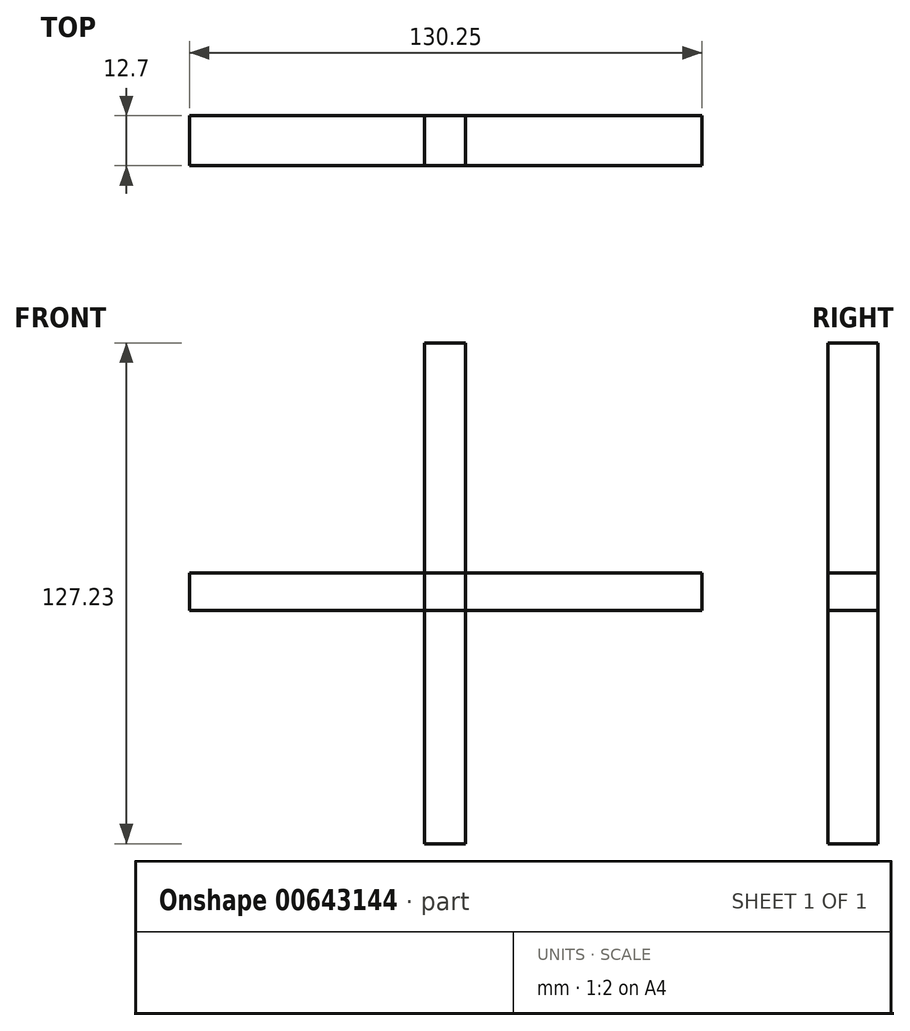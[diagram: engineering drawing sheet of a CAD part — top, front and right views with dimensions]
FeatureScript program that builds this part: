
annotation { "Feature Type Name" : "Feature", "Feature Type Description" : "" }
export const myFeature = defineFeature(function(context is Context, id is Id, definition is map)
    precondition{}
    {
        {
            var Q0;
            Q0=qCreatedBy(makeId("Front.planeOp"),FACE);
            var sketch = newSketch(context, id + "F0", { "sketchPlane" : qUnion([Q0])});
            skLineSegment(sketch, "E0.bottom", {"start": v(10.38, 0) * mm, "end": v(0, 0) * mm});
            skLineSegment(sketch, "E0.top", {"start": v(10.38, 58.5) * mm, "end": v(0, 58.5) * mm});
            skLineSegment(sketch, "E0.left", {"start": v(10.38, 0) * mm, "end": v(10.38, 58.5) * mm});
            skLineSegment(sketch, "E0.right", {"start": v(0, 0) * mm, "end": v(0, 58.5) * mm});
            skLineSegment(sketch, "E1.bottom", {"start": v(10.38, 0) * mm, "end": v(70.54, 0) * mm});
            skLineSegment(sketch, "E1.top", {"start": v(10.38, -9.47) * mm, "end": v(70.54, -9.47) * mm});
            skLineSegment(sketch, "E1.left", {"start": v(10.38, 0) * mm, "end": v(10.38, -9.47) * mm});
            skLineSegment(sketch, "E1.right", {"start": v(70.54, 0) * mm, "end": v(70.54, -9.47) * mm});
            skLineSegment(sketch, "E2.bottom", {"start": v(10.38, -9.47) * mm, "end": v(0, -9.47) * mm});
            skLineSegment(sketch, "E2.top", {"start": v(10.38, -68.73) * mm, "end": v(0, -68.73) * mm});
            skLineSegment(sketch, "E2.left", {"start": v(10.38, -9.47) * mm, "end": v(10.38, -68.73) * mm});
            skLineSegment(sketch, "E2.right", {"start": v(0, -9.47) * mm, "end": v(0, -68.73) * mm});
            skLineSegment(sketch, "E3.bottom", {"start": v(0, -9.47) * mm, "end": v(-59.7, -9.47) * mm});
            skLineSegment(sketch, "E3.top", {"start": v(0, 0) * mm, "end": v(-59.7, 0) * mm});
            skLineSegment(sketch, "E3.left", {"start": v(0, -9.47) * mm, "end": v(0, 0) * mm});
            skLineSegment(sketch, "E3.right", {"start": v(-59.7, -9.47) * mm, "end": v(-59.7, 0) * mm});
            skSolve(sketch);
        }
        {
            var Q0;
            Q0=makeQuery(id+"F0.imprint","IMPRINT",FACE,{"disambiguationData":[TD([[makeQuery(id+"F0.imprint","IMPRINT",EDGE,{"derivedFrom":sQuery(id+"F0.wireOp",EDGE,"E3.bottom")}),-1.0]])]});
            var Q1;
            Q1=makeQuery(id+"F0.imprint","IMPRINT",FACE,{"disambiguationData":[TD([[makeQuery(id+"F0.imprint","IMPRINT",EDGE,{"derivedFrom":sQuery(id+"F0.wireOp",EDGE,"E0.bottom")}),-1.0]])]});
            var Q2;
            Q2=makeQuery(id+"F0.imprint","IMPRINT",FACE,{"disambiguationData":[TD([[makeQuery(id+"F0.imprint","IMPRINT",EDGE,{"derivedFrom":sQuery(id+"F0.wireOp",EDGE,"E1.bottom")}),-1.0]])]});
            var Q3;
            Q3=makeQuery(id+"F0.imprint","IMPRINT",FACE,{"disambiguationData":[TD([[makeQuery(id+"F0.imprint","IMPRINT",EDGE,{"derivedFrom":sQuery(id+"F0.wireOp",EDGE,"E2.bottom")}),1.0]])]});
            extrude(context, id + "F1", {"entities" : qUnion([Q0, Q1, Q2, Q3]), "depth" : 12.7 * mm, "offsetDistance" : 25.4 * mm});
        }
        {
            var Q0;
            Q0=makeQuery(id+"F0.imprint","IMPRINT",FACE,{"disambiguationData":[TD([[makeQuery(id+"F0.imprint","IMPRINT",EDGE,{"derivedFrom":sQuery(id+"F0.wireOp",EDGE,"E0.bottom")}),1.0]])]});
            extrude(context, id + "F2", {"entities" : qUnion([Q0]), "depth" : 12.7 * mm, "offsetDistance" : 25.4 * mm});
        }
        {
            var Q0;
            Q0=qCreatedBy(makeId("Front.planeOp"),FACE);
            var sketch = newSketch(context, id + "F3", { "sketchPlane" : qUnion([Q0])});
            skArc(sketch, "E4", {"start": v(11.28, 14.59) * mm, "mid": v(14.69, 5.14) * mm, "end": v(23.31, 0) * mm});
            skArc(sketch, "E5", {"start": v(10.98, 28.42) * mm, "mid": v(16.27, 10.82) * mm, "end": v(31.13, 0) * mm});
            skArc(sketch, "E6", {"start": v(11.28, 40.46) * mm, "mid": v(21.41, 16.87) * mm, "end": v(40.76, 0) * mm});
            skArc(sketch, "E7", {"start": v(11.28, 48.58) * mm, "mid": v(26.05, 21.99) * mm, "end": v(47.07, 0) * mm});
            skArc(sketch, "E8", {"start": v(11.28, 55.2) * mm, "mid": v(34.23, 27.3) * mm, "end": v(57.9, 0) * mm});
            skArc(sketch, "E9", {"start": v(-8.87, 0) * mm, "mid": v(-2.6, 6.2) * mm, "end": v(0, 14.63) * mm});
            skArc(sketch, "E10", {"start": v(-18.8, 0) * mm, "mid": v(-5.12, 11.2) * mm, "end": v(0, 28.12) * mm});
            skArc(sketch, "E11", {"start": v(-26.92, 0) * mm, "mid": v(-10.4, 18.2) * mm, "end": v(0, 40.46) * mm});
            skArc(sketch, "E12", {"start": v(-39.55, 0) * mm, "mid": v(-16.13, 21.32) * mm, "end": v(0, 48.58) * mm});
            skArc(sketch, "E13", {"start": v(0, 56.1) * mm, "mid": v(-25.33, 28.57) * mm, "end": v(-49.48, 0) * mm});
            skSolve(sketch);
        }
        {
            var Q0;
            Q0=sQuery(id+"F3.wireOp",EDGE,"E13");
            var Q1;
            Q1=sQuery(id+"F3.wireOp",EDGE,"E8");
            var Q2;
            Q2=sQuery(id+"F3.wireOp",EDGE,"E12");
            var Q3;
            Q3=sQuery(id+"F3.wireOp",EDGE,"E11");
            var Q4;
            Q4=sQuery(id+"F3.wireOp",EDGE,"E10");
            var Q5;
            Q5=sQuery(id+"F3.wireOp",EDGE,"E9");
            var Q6;
            Q6=sQuery(id+"F3.wireOp",EDGE,"E4");
            var Q7;
            Q7=sQuery(id+"F3.wireOp",EDGE,"E5");
            var Q8;
            Q8=sQuery(id+"F3.wireOp",EDGE,"E6");
            var Q9;
            Q9=sQuery(id+"F3.wireOp",EDGE,"E7");
            extrude(context, id + "F4", {"bodyType" : ToolBodyType.SURFACE, "surfaceEntities" : qUnion([Q0, Q1, Q2, Q3, Q4, Q5, Q6, Q7, Q8, Q9]), "depth" : 12.7 * mm, "offsetDistance" : 25.4 * mm});
        }
        {
            var Q0;
            Q0=makeQuery(id+"F4.opExtrude","SWEPT_BODY",BODY,{"disambiguationData":[OSD([sQuery(id+"F3.wireOp",EDGE,"E9")])]});
            var Q1;
            Q1=makeQuery(id+"F4.opExtrude","SWEPT_BODY",BODY,{"disambiguationData":[OSD([sQuery(id+"F3.wireOp",EDGE,"E12")])]});
            var Q2;
            Q2=makeQuery(id+"F4.opExtrude","SWEPT_BODY",BODY,{"disambiguationData":[OSD([sQuery(id+"F3.wireOp",EDGE,"E13")])]});
            var Q3;
            Q3=makeQuery(id+"F4.opExtrude","SWEPT_BODY",BODY,{"disambiguationData":[OSD([sQuery(id+"F3.wireOp",EDGE,"E11")])]});
            var Q4;
            Q4=makeQuery(id+"F4.opExtrude","SWEPT_BODY",BODY,{"disambiguationData":[OSD([sQuery(id+"F3.wireOp",EDGE,"E10")])]});
            var Q5;
            Q5=makeQuery(id+"F4.opExtrude","SWEPT_BODY",BODY,{"disambiguationData":[OSD([sQuery(id+"F3.wireOp",EDGE,"E4")])]});
            var Q6;
            Q6=makeQuery(id+"F4.opExtrude","SWEPT_BODY",BODY,{"disambiguationData":[OSD([sQuery(id+"F3.wireOp",EDGE,"E6")])]});
            var Q7;
            Q7=makeQuery(id+"F4.opExtrude","SWEPT_BODY",BODY,{"disambiguationData":[OSD([sQuery(id+"F3.wireOp",EDGE,"E5")])]});
            var Q8;
            Q8=makeQuery(id+"F4.opExtrude","SWEPT_BODY",BODY,{"disambiguationData":[OSD([sQuery(id+"F3.wireOp",EDGE,"E7")])]});
            var Q9;
            Q9=makeQuery(id+"F4.opExtrude","SWEPT_BODY",BODY,{"disambiguationData":[OSD([sQuery(id+"F3.wireOp",EDGE,"E8")])]});
            var Q10;
            Q10=qCreatedBy(makeId("Top.planeOp"),FACE);
            mirror(context, id + "F5", {"entities" : qUnion([Q0, Q1, Q2, Q3, Q4, Q5, Q6, Q7, Q8, Q9]), "mirrorPlane" : qUnion([Q10])});
        }
    });
